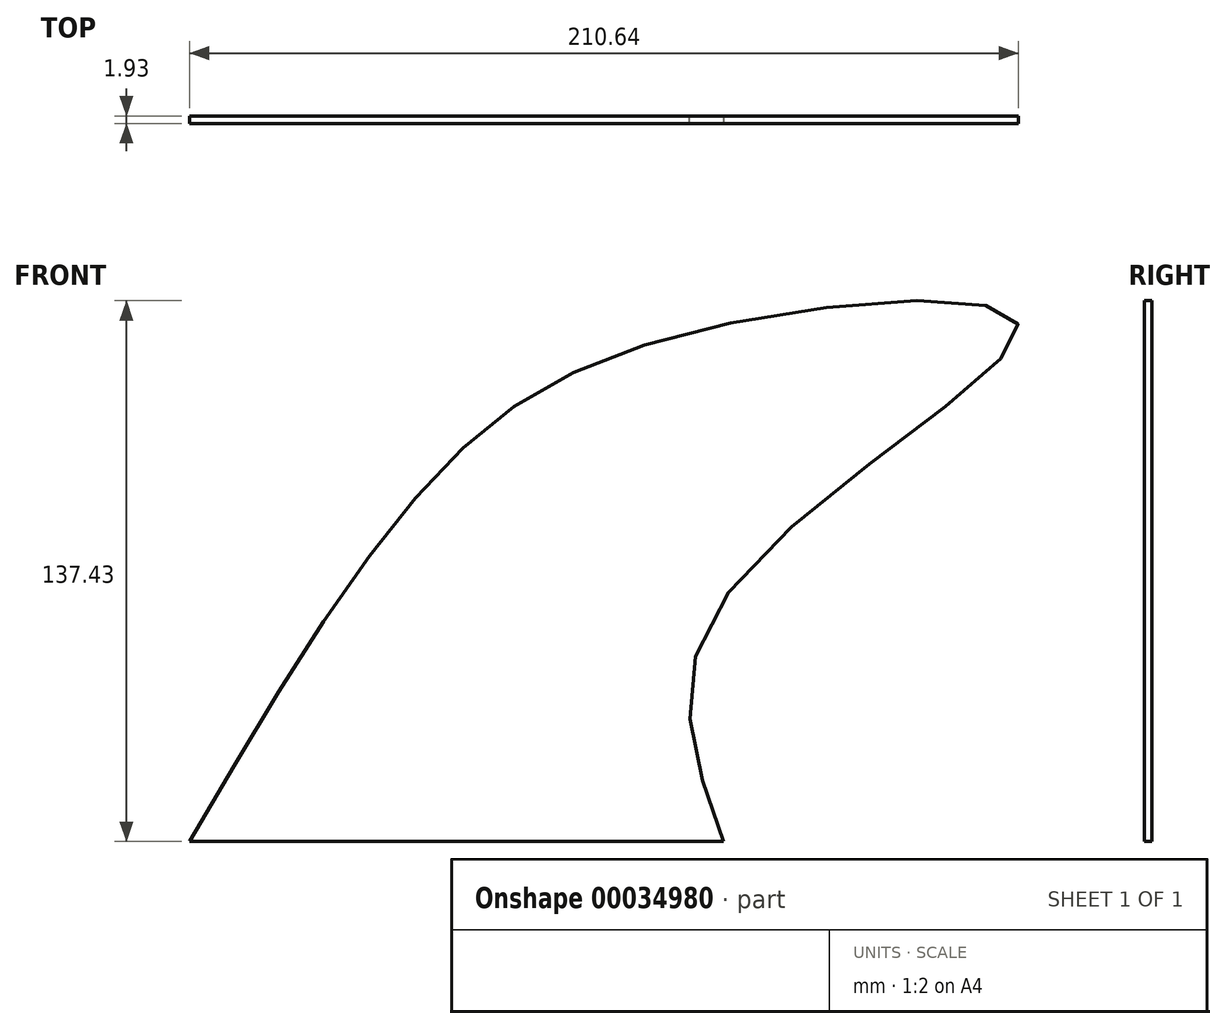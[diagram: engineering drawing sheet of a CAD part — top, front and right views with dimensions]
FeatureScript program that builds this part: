
annotation { "Feature Type Name" : "Feature", "Feature Type Description" : "" }
export const myFeature = defineFeature(function(context is Context, id is Id, definition is map)
    precondition{}
    {
        {
            var Q0;
            Q0=qCreatedBy(makeId("Front.planeOp"),FACE);
            var sketch = newSketch(context, id + "F0", { "sketchPlane" : qUnion([Q0])});
            skLineSegment(sketch, "E0", {"start": v(-65.73, -61.66) * mm, "end": v(70, -61.66) * mm});
            skFitSpline(sketch, "E1", {"points": [v(70, -61.66) * mm, v(70, 0) * mm, v(144.89, 69.19) * mm, v(61.46, 67.76) * mm, v(-6.72, 27.47) * mm, v(-65.73, -61.66) * mm], "startDerivative": vector(-133.47, 355.97) * mm, "endDerivative": vector(-260.38, -444.34) * mm});
            skSolve(sketch);
        }
        {
            var Q0;
            Q0=makeQuery(id+"F0.imprint","IMPRINT",FACE,{"disambiguationData":[TD([[makeQuery(id+"F0.imprint","IMPRINT",EDGE,{"derivedFrom":sQuery(id+"F0.wireOp",EDGE,"E0")}),1.0]])]});
            extrude(context, id + "F1", {"entities" : qUnion([Q0]), "oppositeDirection" : true, "depth" : 1.93 * mm});
        }
    });
